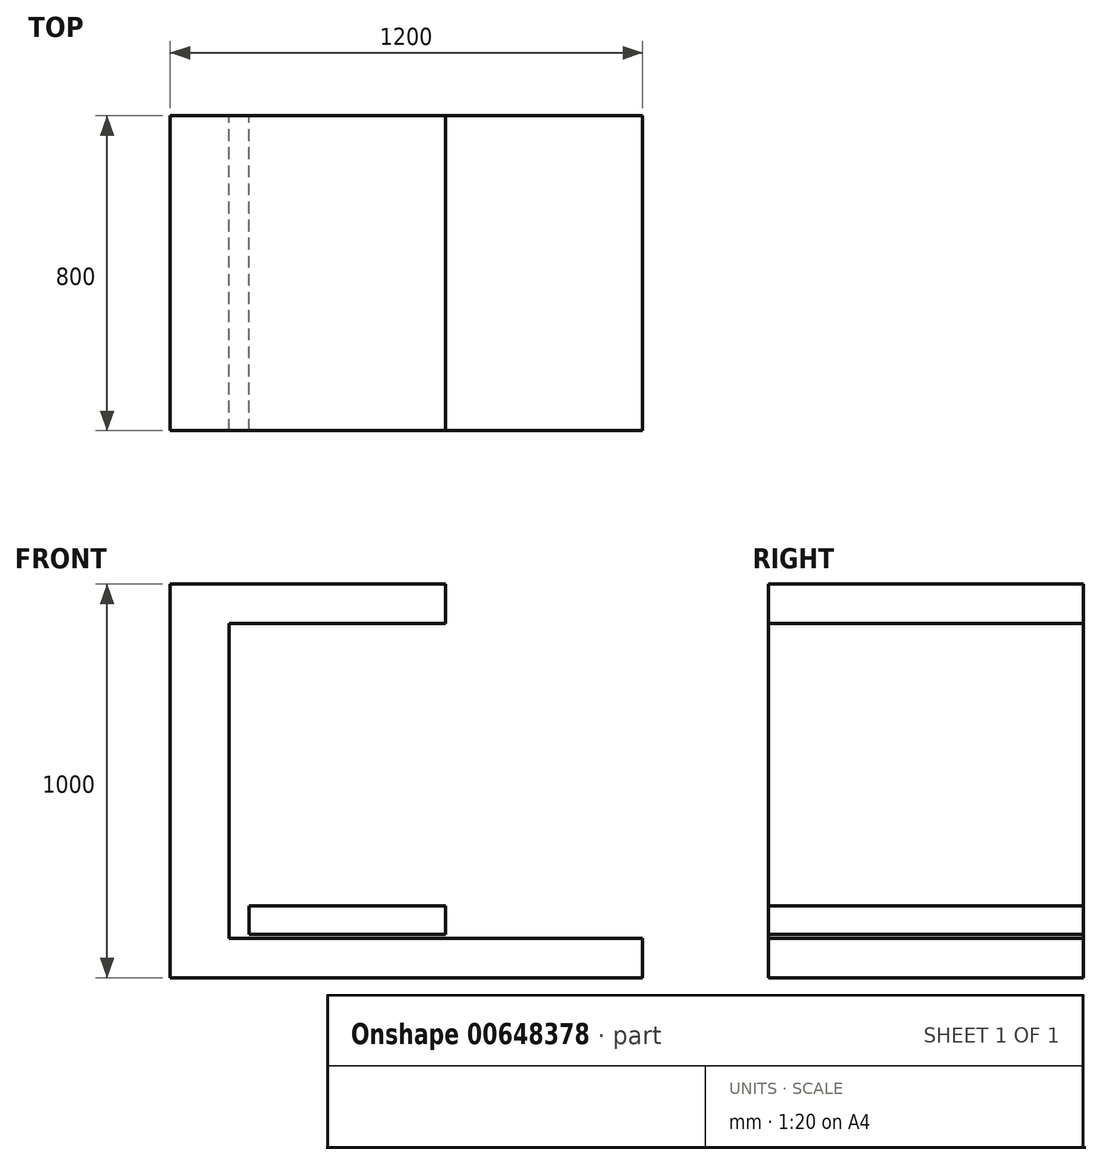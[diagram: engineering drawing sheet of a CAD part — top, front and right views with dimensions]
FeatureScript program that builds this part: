
annotation { "Feature Type Name" : "Feature", "Feature Type Description" : "" }
export const myFeature = defineFeature(function(context is Context, id is Id, definition is map)
    precondition{}
    {
        {
            var Q0;
            Q0=qCreatedBy(makeId("Front.planeOp"),FACE);
            var sketch = newSketch(context, id + "F0", { "sketchPlane" : qUnion([Q0])});
            skLineSegment(sketch, "E0.bottom", {"start": v(-600, 500) * mm, "end": v(-450, 500) * mm});
            skLineSegment(sketch, "E0.top", {"start": v(-600, -500) * mm, "end": v(-450, -500) * mm});
            skLineSegment(sketch, "E0.left", {"start": v(-600, 500) * mm, "end": v(-600, -500) * mm});
            skLineSegment(sketch, "E0.right", {"start": v(-450, 500) * mm, "end": v(-450, -500) * mm});
            skLineSegment(sketch, "E1.bottom", {"start": v(-450, -400) * mm, "end": v(600, -400) * mm});
            skLineSegment(sketch, "E1.top", {"start": v(-450, -500) * mm, "end": v(600, -500) * mm});
            skLineSegment(sketch, "E1.left", {"start": v(-450, -400) * mm, "end": v(-450, -500) * mm});
            skLineSegment(sketch, "E1.right", {"start": v(600, -400) * mm, "end": v(600, -500) * mm});
            skLineSegment(sketch, "E2.bottom", {"start": v(-400, -317.97) * mm, "end": v(100, -317.97) * mm});
            skLineSegment(sketch, "E2.top", {"start": v(-400, -390) * mm, "end": v(100, -390) * mm});
            skLineSegment(sketch, "E2.left", {"start": v(-400, -317.97) * mm, "end": v(-400, -390) * mm});
            skLineSegment(sketch, "E2.right", {"start": v(100, -317.97) * mm, "end": v(100, -390) * mm});
            skLineSegment(sketch, "E3.bottom", {"start": v(-450, 500) * mm, "end": v(100, 500) * mm});
            skLineSegment(sketch, "E3.top", {"start": v(-450, 400) * mm, "end": v(100, 400) * mm});
            skLineSegment(sketch, "E3.left", {"start": v(-450, 500) * mm, "end": v(-450, 400) * mm});
            skLineSegment(sketch, "E3.right", {"start": v(100, 500) * mm, "end": v(100, 400) * mm});
            skLineSegment(sketch, "E4.bottom", {"start": v(-750, 750) * mm, "end": v(750, 750) * mm, "construction": true});
            skLineSegment(sketch, "E4.top", {"start": v(-750, -750) * mm, "end": v(750, -750) * mm, "construction": true});
            skLineSegment(sketch, "E4.left", {"start": v(-750, 750) * mm, "end": v(-750, -750) * mm, "construction": true});
            skLineSegment(sketch, "E4.right", {"start": v(750, 750) * mm, "end": v(750, -750) * mm, "construction": true});
            skLineSegment(sketch, "E5", {"start": v(0, 0) * mm, "end": v(0, 750) * mm, "construction": true});
            skLineSegment(sketch, "E6", {"start": v(0, 0) * mm, "end": v(-750, 0) * mm, "construction": true});
            skLineSegment(sketch, "E7", {"start": v(-600, -500) * mm, "end": v(-750, -500) * mm, "construction": true});
            skLineSegment(sketch, "E8", {"start": v(100, 400) * mm, "end": v(100, 354.54) * mm});
            skLineSegment(sketch, "E9", {"start": v(100, 354.54) * mm, "end": v(100, -317.97) * mm, "construction": true});
            skLineSegment(sketch, "E10", {"start": v(0, 0) * mm, "end": v(100, 0) * mm, "construction": true});
            skSolve(sketch);
        }
        {
            var Q0;
            {var subQ4=sQuery(id+"F0.wireOp",EDGE,"E0.bottom");Q0=makeQuery(id+"F0.imprint","IMPRINT",FACE,{"disambiguationData":[TD([[makeQuery(id+"F0.imprint","IMPRINT",EDGE,{"derivedFrom":subQ4}),-1.0]])]});}
            var Q1;
            {var subQ0=sQuery(id+"F0.wireOp",EDGE,"E3.bottom");Q1=makeQuery(id+"F0.imprint","IMPRINT",FACE,{"disambiguationData":[TD([[makeQuery(id+"F0.imprint","IMPRINT",EDGE,{"derivedFrom":subQ0}),-1.0]])]});}
            var Q2;
            {var subQ2=sQuery(id+"F0.wireOp",EDGE,"E1.bottom");Q2=makeQuery(id+"F0.imprint","IMPRINT",FACE,{"disambiguationData":[TD([[makeQuery(id+"F0.imprint","IMPRINT",EDGE,{"derivedFrom":subQ2}),-1.0]])]});}
            var Q3;
            Q3=makeQuery(id+"F0.imprint","IMPRINT",FACE,{"disambiguationData":[TD([[makeQuery(id+"F0.imprint","IMPRINT",EDGE,{"derivedFrom":sQuery(id+"F0.wireOp",EDGE,"E2.bottom")}),-1.0]])]});
            extrude(context, id + "F1", {"entities" : qUnion([Q0, Q1, Q2, Q3]), "depth" : 800 * mm, "offsetDistance" : 25 * mm});
        }
    });
